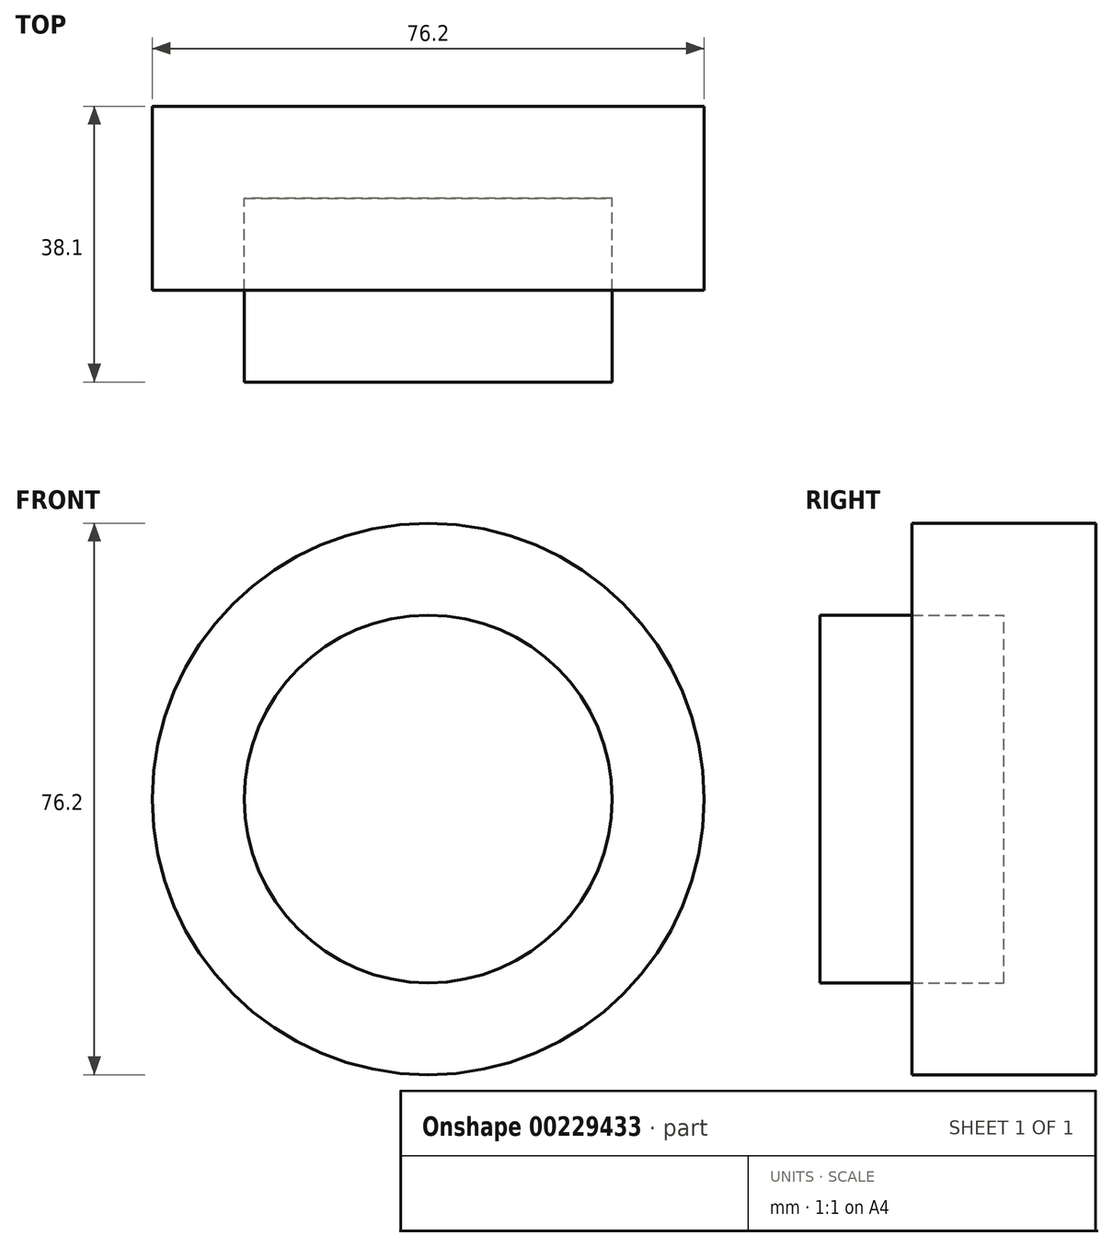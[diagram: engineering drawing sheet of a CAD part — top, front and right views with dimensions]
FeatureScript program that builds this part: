
annotation { "Feature Type Name" : "Feature", "Feature Type Description" : "" }
export const myFeature = defineFeature(function(context is Context, id is Id, definition is map)
    precondition{}
    {
        {
            var Q0;
            Q0=qCreatedBy(makeId("Front.planeOp"),FACE);
            var sketch = newSketch(context, id + "F0", { "sketchPlane" : qUnion([Q0])});
            skCircle(sketch, "E0", {"center": v(0, 0) * mm, "radius": 38.1 * mm});
            skSolve(sketch);
        }
        {
            var Q0;
            Q0=makeQuery(id+"F0.imprint","IMPRINT",FACE,{"disambiguationData":[TD([[makeQuery(id+"F0.imprint","IMPRINT",EDGE,{"derivedFrom":sQuery(id+"F0.wireOp",EDGE,"E0")}),1.0]])]});
            extrude(context, id + "F1", {"entities" : qUnion([Q0]), "depth" : 25.4 * mm});
        }
        {
            var Q0;
            Q0=makeQuery(id+"F1.opExtrude","CAP_FACE",FACE,{"disambiguationData":[OSD([sQuery(id+"F0.wireOp",EDGE,"E0")])],"isStart":false});
            cPlane(context, id + "F4", {"entities" : qUnion([Q0]), "cplaneType" : CPlaneType.OFFSET, "offset" : 12.7 * mm, "oppositeDirection" : true, "width" : 152.4 * mm, "height" : 152.4 * mm});
        }
        {
            var Q0;
            Q0=qCreatedBy(id+"F4.planeOp",FACE);
            var sketch = newSketch(context, id + "F2", { "sketchPlane" : qUnion([Q0])});
            skCircle(sketch, "E1", {"center": v(0, 0) * mm, "radius": 25.4 * mm});
            skSolve(sketch);
        }
        {
            var Q0;
            Q0=makeQuery(id+"F2.imprint","IMPRINT",FACE,{"disambiguationData":[TD([[makeQuery(id+"F2.imprint","IMPRINT",EDGE,{"derivedFrom":sQuery(id+"F2.wireOp",EDGE,"E1")}),1.0]])]});
            extrude(context, id + "F3", {"entities" : qUnion([Q0]), "depth" : 25.4 * mm});
        }
    });
